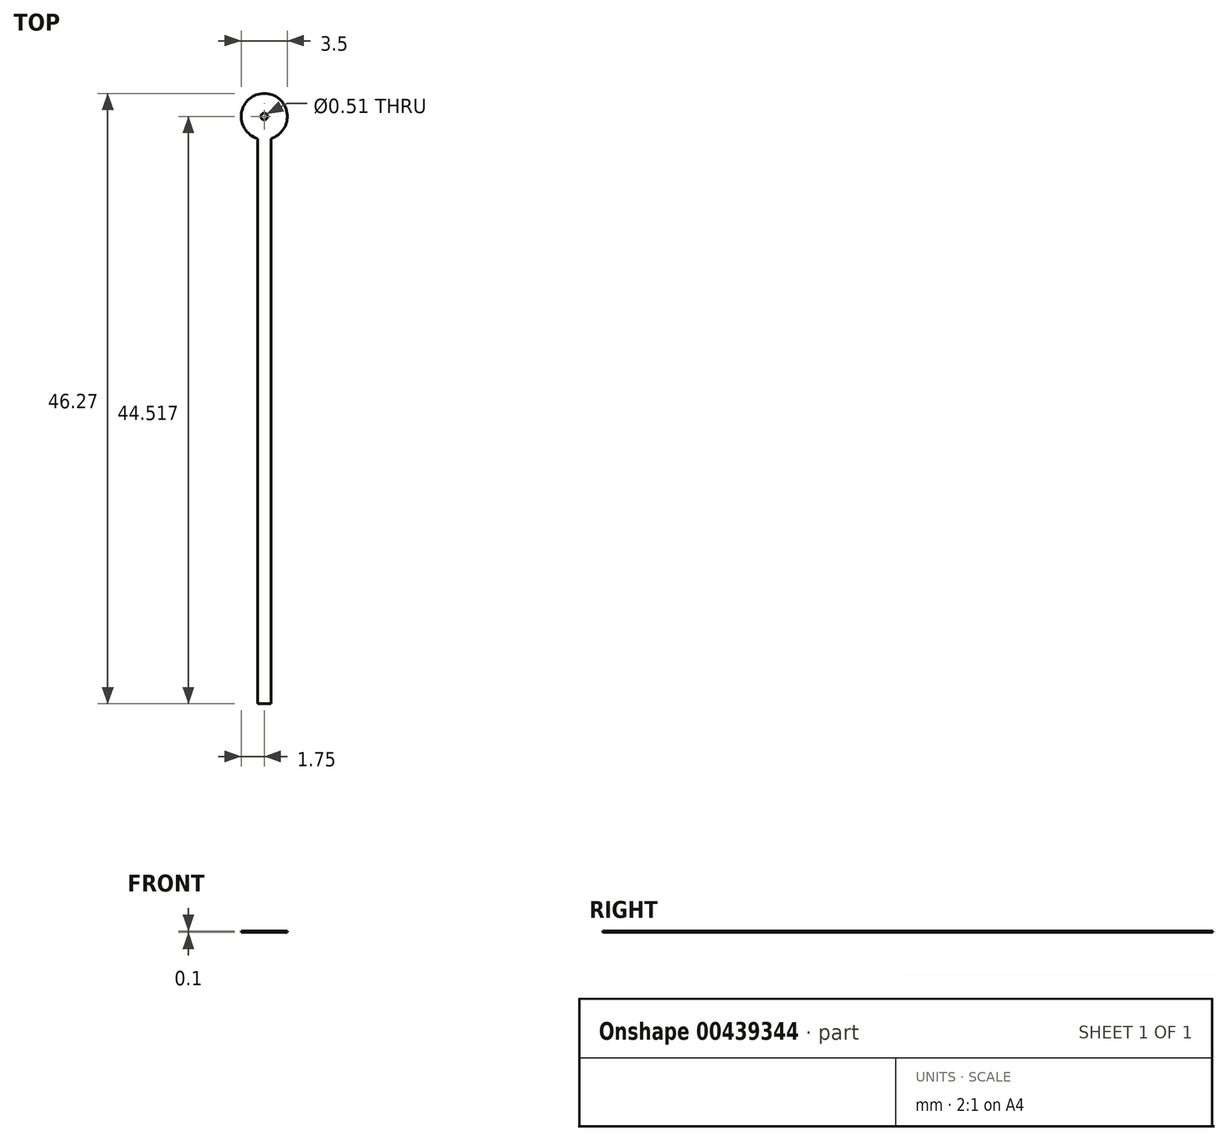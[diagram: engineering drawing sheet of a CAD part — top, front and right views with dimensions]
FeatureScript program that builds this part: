
annotation { "Feature Type Name" : "Feature", "Feature Type Description" : "" }
export const myFeature = defineFeature(function(context is Context, id is Id, definition is map)
    precondition{}
    {
        {
            var Q0;
            Q0=qCreatedBy(makeId("Top.planeOp"),FACE);
            var sketch = newSketch(context, id + "F0", { "sketchPlane" : qUnion([Q0])});
            skLineSegment(sketch, "E0", {"start": v(0, 0) * mm, "end": v(0, 42.84) * mm});
            skLineSegment(sketch, "E1", {"start": v(1, 42.84) * mm, "end": v(1, 0) * mm});
            skLineSegment(sketch, "E2", {"start": v(1, 0) * mm, "end": v(0, 0) * mm});
            skArc(sketch, "E3", {"start": v(1, 42.84) * mm, "mid": v(0.5, 46.27) * mm, "end": v(0, 42.84) * mm});
            skPoint(sketch, "E3.centerSnap0", {"position": v(0.5, 42.84) * mm});
            skCircle(sketch, "E4", {"center": v(0.5, 44.52) * mm, "radius": 0.26 * mm});
            skSolve(sketch);
        }
        {
            var Q0;
            Q0 = qSketchRegion(id + "F0", true);
            extrude(context, id + "F1", {"entities" : qUnion([Q0]), "depth" : 0.1 * mm});
        }
    });
